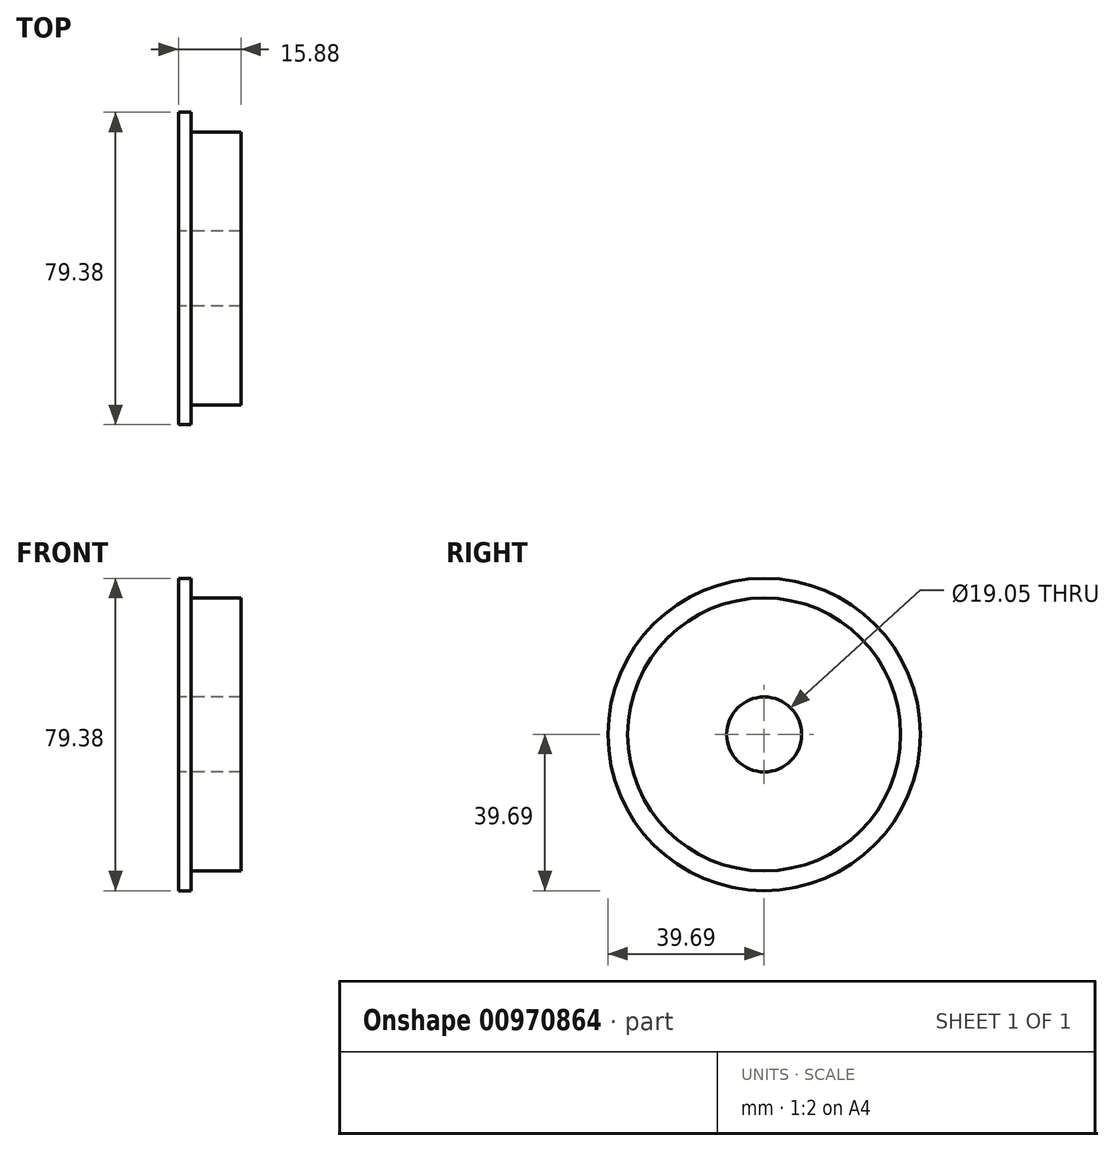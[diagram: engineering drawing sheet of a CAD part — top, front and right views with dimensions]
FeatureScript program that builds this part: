
annotation { "Feature Type Name" : "Feature", "Feature Type Description" : "" }
export const myFeature = defineFeature(function(context is Context, id is Id, definition is map)
    precondition{}
    {
        {
            var Q0;
            Q0=qCreatedBy(makeId("Right.planeOp"),FACE);
            var sketch = newSketch(context, id + "F0", { "sketchPlane" : qUnion([Q0])});
            skCircle(sketch, "E0", {"center": v(0, 0) * mm, "radius": 34.67 * mm});
            skCircle(sketch, "E1", {"center": v(0, 0) * mm, "radius": 9.53 * mm});
            skSolve(sketch);
        }
        {
            var Q0;
            Q0=makeQuery(id+"F0.imprint","IMPRINT",FACE,{"disambiguationData":[TD([[makeQuery(id+"F0.imprint","IMPRINT",EDGE,{"derivedFrom":sQuery(id+"F0.wireOp",EDGE,"E0")}),1.0]])]});
            extrude(context, id + "F1", {"entities" : qUnion([Q0]), "depth" : 12.7 * mm, "offsetDistance" : 25.4 * mm});
        }
        {
            var Q0;
            Q0=makeQuery(id+"F1.opExtrude","CAP_FACE",FACE,{"disambiguationData":[OSD([sQuery(id+"F0.wireOp",EDGE,"E0"),sQuery(id+"F0.wireOp",EDGE,"E1")])],"isStart":true});
            var sketch = newSketch(context, id + "F2", { "sketchPlane" : qUnion([Q0])});
            skCircle(sketch, "E2", {"center": v(0, 0) * mm, "radius": 39.69 * mm});
            skSolve(sketch);
        }
        {
            var Q0;
            Q0=makeQuery(id+"F2.imprint","IMPRINT",FACE,{"disambiguationData":[TD([[makeQuery(id+"F2.imprint","IMPRINT",EDGE,{"derivedFrom":sQuery(id+"F2.wireOp",EDGE,"E2")}),1.0]])]});
            extrude(context, id + "F3", {"entities" : qUnion([Q0]), "operationType" : NewBodyOperationType.ADD, "depth" : 3.17 * mm, "offsetDistance" : 25.4 * mm});
        }
        {
            var Q0;
            Q0=makeQuery(id+"F1.opExtrude","CAP_FACE",FACE,{"disambiguationData":[OSD([sQuery(id+"F0.wireOp",EDGE,"E0"),sQuery(id+"F0.wireOp",EDGE,"E1")])],"isStart":true});
            extrude(context, id + "F4", {"entities" : qUnion([Q0]), "operationType" : NewBodyOperationType.ADD, "depth" : 3.17 * mm, "offsetDistance" : 25.4 * mm});
        }
    });
